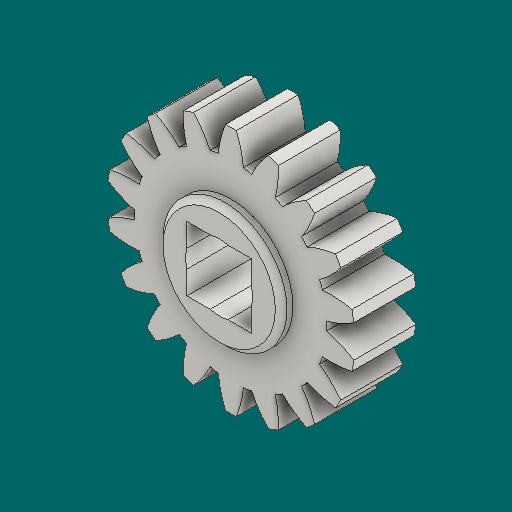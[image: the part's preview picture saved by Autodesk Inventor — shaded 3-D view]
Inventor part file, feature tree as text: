
AUTODESK INVENTOR PART (.ipt)
format: ipt  version: 2023.1 (Build 271208000, 208)  size: 324,608 bytes
history: native  units: in
note: dims shown in document units (in); Inventor stores cm internally (conversion verified against a paired STEP export)
features: other x12, sketch x4, plane x3
ambient origin geometry x8: Origin, YZ Plane, XZ Plane, XY Plane, X Axis, Y Axis, Z Axis, Center Point
bodies: Solid1 (feature_tree)
feature tree (19):
  other  "Spur Gear1"
  other  "Solid1::Spur Gear1"
  other  "TaggingFeature1"
  sketch  "Sketch1"  dims[d0=0.3937in]
  sketch  "Sketch2"  dims[d9=0.0in]
  sketch  "Sketch3"  dims[d14=0.0in]
  sketch  "Sketch4"  dims[d15=0.9in d16=0.0in d17=0.0in d18=0.0in d19=0.9in]
  plane  "XZ Plane_1"
  plane  "Work Plane2"
  plane  "Work Plane3"
  other  "Srf1"
  other  "Srf1::Derived"
  other  "Start plane iMate"
  other  "Distance iMate"
  other  "Position iMate"
  other  "Mesh iMate"
  other  "Axis iMate"
  other  "Mesh iMate2"
  other  "Align iMate"
